# Revit family: Faucet-Kitchen-American_Standard-Studio_S-4803100_Series
name_source: partatom
category: Plumbing Fixtures
units: mm (PartAtom-declared; Revit-internal decimal feet)

## family parameters
Always vertical = No
Cut with Voids When Loaded = No
OmniClass Number = 23.45.55.14
OmniClass Title = Single Faucets
Part Type = Normal
Room Calculation Point = No
Round Connector Dimension = Use Diameter
Shared = Yes
Work Plane-Based = Yes

## types (3) — shared parameters
ADA Compliant = Yes
Assembly Code = D2020300
CEC Compliant = Yes
CW Connection = No
CWFU = 1.5
CalGreen Compliant = Yes
Deck Height = 1/4"
Deck Length = 2 7/16"
Deck Plate = No
Deck Width = 4"
Default Elevation = 0"
Description = Studio® S Pull-Out Dual-Spray Kitchen Faucet
HW Connection = No
HWFU = 1.5
Height = 10 7/8"
Installation Type = Deck Mounted
Length = 9 1/16"
Manufacturer = American Standard
No Deck Plate = Yes
Optional 70204P0 4" Deck Plate = No
Optional 70208P0 8" Deck Plate = No
Price = Prices may vary. Please consult Manufacturer Representative for most up-to-date price list.
Product Documentation Link = https://americanstandard.box.com
Product Page URL = https://www.americanstandard-us.com
Revised Date = 03/03/2022
Tempered Water Connection = Yes
Tempered Water Connection Diameter = 3/8"
URL = https://www.americanstandard-us.com
Vent Connection = No
WFU = 2
Warranty Information = Limited Lifetime Function and Finish Warranty
Waste Connection = No
Width = 2 3/16"

## per-type parameters (varying)
| type | Finish | IAPMO Compliance | Material |
| 4803100.002 | Brass-American Standard-002-Polished Chrome |  | Brass-American Standard-002-Polished Chrome |
| 4803100.075 | Brass-American Standard-075-Stainless Steel |  | Brass-American Standard-075-Stainless Steel |
| 4803100.243 | Metal-American Standard-243-Matte Black | NSF 372, ANSI A117.1, ASME A112.18.1/CSA B125.1, NSF/ANSI 61, Section 9 | Metal-American Standard-243-Matte Black |

note: column(s) folded — value = type name in every type: Model

## geometry (parser evidence)
native form markers: Sweep x2
no freeform markers — native parametric forms only
